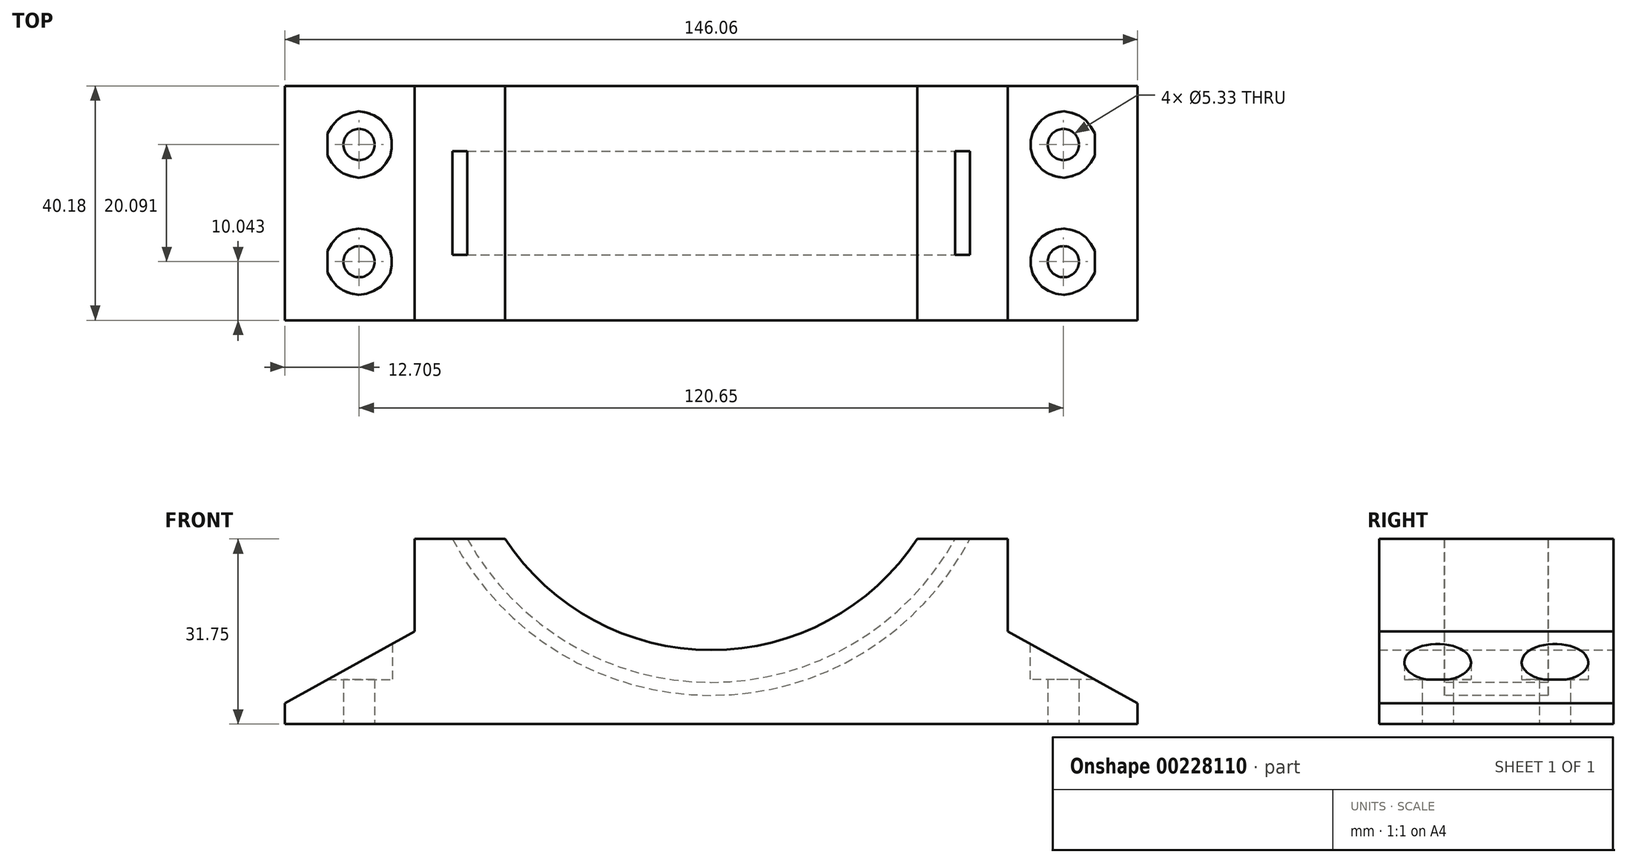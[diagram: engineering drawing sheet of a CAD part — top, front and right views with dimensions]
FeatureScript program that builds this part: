
annotation { "Feature Type Name" : "Feature", "Feature Type Description" : "" }
export const myFeature = defineFeature(function(context is Context, id is Id, definition is map)
    precondition{}
    {
        {
            var Q0;
            Q0=qCreatedBy(makeId("Front.planeOp"),FACE);
            var sketch = newSketch(context, id + "F0", { "sketchPlane" : qUnion([Q0])});
            skLineSegment(sketch, "E0.bottom", {"start": v(50.8, 0) * mm, "end": v(-50.8, 0) * mm});
            skLineSegment(sketch, "E0.top", {"start": v(50.8, 31.75) * mm, "end": v(-50.8, 31.75) * mm});
            skLineSegment(sketch, "E0.left", {"start": v(50.8, 0) * mm, "end": v(50.8, 31.75) * mm});
            skLineSegment(sketch, "E0.right", {"start": v(-50.8, 0) * mm, "end": v(-50.8, 31.75) * mm});
            skPoint(sketch, "E0.middle", {"position": v(0, 15.88) * mm});
            skCircle(sketch, "E1", {"center": v(0, 54.94) * mm, "radius": 42.24 * mm});
            skLineSegment(sketch, "E2", {"start": v(0, 76.33) * mm, "end": v(0, 0) * mm, "construction": true});
            skLineSegment(sketch, "E3", {"start": v(-50.8, 15.88) * mm, "end": v(-73.03, 3.58) * mm});
            skLineSegment(sketch, "E4", {"start": v(-73.03, 3.58) * mm, "end": v(-73.03, 0) * mm});
            skLineSegment(sketch, "E5", {"start": v(-73.03, 0) * mm, "end": v(-50.8, 0) * mm});
            skLineSegment(sketch, "E6.MirrorCS", {"start": v(50.8, 15.88) * mm, "end": v(73.02, 3.58) * mm});
            skLineSegment(sketch, "E7.MirrorCS", {"start": v(73.03, 3.58) * mm, "end": v(73.03, 0) * mm});
            skLineSegment(sketch, "E8.MirrorCS", {"start": v(73.03, 0) * mm, "end": v(50.8, 0) * mm});
            skSolve(sketch);
        }
        {
            var Q0;
            {var subQ1=sQuery(id+"F0.wireOp",EDGE,"E0.bottom");Q0=makeQuery(id+"F0.imprint","IMPRINT",FACE,{"disambiguationData":[TD([[makeQuery(id+"F0.imprint","IMPRINT",EDGE,{"derivedFrom":subQ1}),-1.0]])]});}
            var Q1;
            {var subQ2=sQuery(id+"F0.wireOp",EDGE,"E3");Q1=makeQuery(id+"F0.imprint","IMPRINT",FACE,{"disambiguationData":[TD([[makeQuery(id+"F0.imprint","IMPRINT",EDGE,{"derivedFrom":subQ2}),1.0]])]});}
            var Q2;
            {var subQ2=sQuery(id+"F0.wireOp",EDGE,"E6.MirrorCS");Q2=makeQuery(id+"F0.imprint","IMPRINT",FACE,{"disambiguationData":[TD([[makeQuery(id+"F0.imprint","IMPRINT",EDGE,{"derivedFrom":subQ2}),-1.0]])]});}
            extrude(context, id + "F1", {"entities" : qUnion([Q0, Q1, Q2]), "depth" : 40.18 * mm});
        }
        {
            var Q0;
            {var subQ0=sQuery(id+"F0.wireOp",EDGE,"E0.top");Q0=makeQuery(id+"F1.opExtrude","SWEPT_FACE",FACE,{"disambiguationData":[OSD([subQ0]),TDD([makeQuery(id+"F0.imprint","IMPRINT",EDGE,{"disambiguationData":[TD([[makeQuery(id+"F0.imprint","INTERSECT",VERTEX,{"derivedFrom":[subQ0,sQuery(id+"F0.wireOp",EDGE,"E0.right")]}),1.0]])],"derivedFrom":subQ0})])]});}
            var sketch = newSketch(context, id + "F2", { "sketchPlane" : qUnion([Q0])});
            skLineSegment(sketch, "E9", {"start": v(-43.05, 0) * mm, "end": v(-43.05, -40.18) * mm, "construction": true});
            skLineSegment(sketch, "E10", {"start": v(-50.8, -20.1) * mm, "end": v(-35.3, -20.1) * mm, "construction": true});
            skLineSegment(sketch, "E11.bottom", {"start": v(-41.78, -28.98) * mm, "end": v(-44.32, -28.98) * mm});
            skLineSegment(sketch, "E11.top", {"start": v(-41.78, -11.2) * mm, "end": v(-44.32, -11.2) * mm});
            skLineSegment(sketch, "E11.left", {"start": v(-41.78, -28.98) * mm, "end": v(-41.78, -11.2) * mm});
            skLineSegment(sketch, "E11.right", {"start": v(-44.32, -28.98) * mm, "end": v(-44.32, -11.2) * mm});
            skPoint(sketch, "E11.middle", {"position": v(-43.05, -20.1) * mm});
            skSolve(sketch);
        }
        {
            var Q0;
            Q0=qCreatedBy(makeId("Right.planeOp"),FACE);
            var sketch = newSketch(context, id + "F3", { "sketchPlane" : qUnion([Q0])});
            skLineSegment(sketch, "E12", {"start": v(0, 54.94) * mm, "end": v(-44.85, 54.94) * mm, "construction": true});
            skSolve(sketch);
        }
        {
            var Q0;
            Q0=makeQuery(id+"F2.imprint","IMPRINT",FACE,{"disambiguationData":[TD([[makeQuery(id+"F2.imprint","IMPRINT",EDGE,{"derivedFrom":sQuery(id+"F2.wireOp",EDGE,"E11.bottom")}),-1.0]])]});
            var Q1;
            Q1=sQuery(id+"F3.wireOp",EDGE,"E12");
            revolve(context, id + "F4", {"operationType" : NewBodyOperationType.REMOVE, "entities" : qUnion([Q0]), "axis" : qUnion([Q1]), "revolveType" : RevolveType.FULL, "oppositeDirection" : true});
        }
        {
            var Q0;
            Q0=qCreatedBy(makeId("Top.planeOp"),FACE);
            var sketch = newSketch(context, id + "F5", { "sketchPlane" : qUnion([Q0])});
            skLineSegment(sketch, "E13", {"start": v(0, 0) * mm, "end": v(0, -39.93) * mm, "construction": true});
            skLineSegment(sketch, "E14", {"start": v(-60.33, 0) * mm, "end": v(-60.33, -40.18) * mm, "construction": true});
            skLineSegment(sketch, "E15", {"start": v(-60.33, -20.1) * mm, "end": v(-73.03, -20.1) * mm, "construction": true});
            skCircle(sketch, "E16", {"center": v(-60.33, -30.14) * mm, "radius": 2.67 * mm});
            skCircle(sketch, "E17.MirrorC", {"center": v(-60.33, -10.05) * mm, "radius": 2.67 * mm});
            skCircle(sketch, "E18.MirrorC", {"center": v(60.33, -30.14) * mm, "radius": 2.67 * mm});
            skCircle(sketch, "E19.MirrorC", {"center": v(60.33, -10.05) * mm, "radius": 2.67 * mm});
            skSolve(sketch);
        }
        {
            var Q0;
            Q0 = qSketchRegion(id + "F5", true);
            extrude(context, id + "F6", {"entities" : qUnion([Q0]), "operationType" : NewBodyOperationType.REMOVE, "depth" : 25.4 * mm});
        }
        {
            var Q0;
            Q0=qCreatedBy(makeId("Top.planeOp"),FACE);
            cPlane(context, id + "F7", {"entities" : qUnion([Q0]), "cplaneType" : CPlaneType.OFFSET, "offset" : 7.62 * mm, "width" : 152.4 * mm, "height" : 152.4 * mm});
        }
        {
            var Q0;
            Q0=qCreatedBy(id+"F7.planeOp",FACE);
            var sketch = newSketch(context, id + "F8", { "sketchPlane" : qUnion([Q0])});
            skCircle(sketch, "E20.0", {"center": v(60.33, -30.14) * mm, "radius": 5.72 * mm});
            skCircle(sketch, "E21.0", {"center": v(60.33, -10.05) * mm, "radius": 5.72 * mm});
            skCircle(sketch, "E22.0", {"center": v(-60.33, -30.14) * mm, "radius": 5.72 * mm});
            skCircle(sketch, "E23.0", {"center": v(-60.33, -10.05) * mm, "radius": 5.72 * mm});
            skSolve(sketch);
        }
        {
            var Q0;
            Q0 = qSketchRegion(id + "F8", true);
            extrude(context, id + "F9", {"entities" : qUnion([Q0]), "operationType" : NewBodyOperationType.REMOVE, "depth" : 25.4 * mm});
        }
    });
